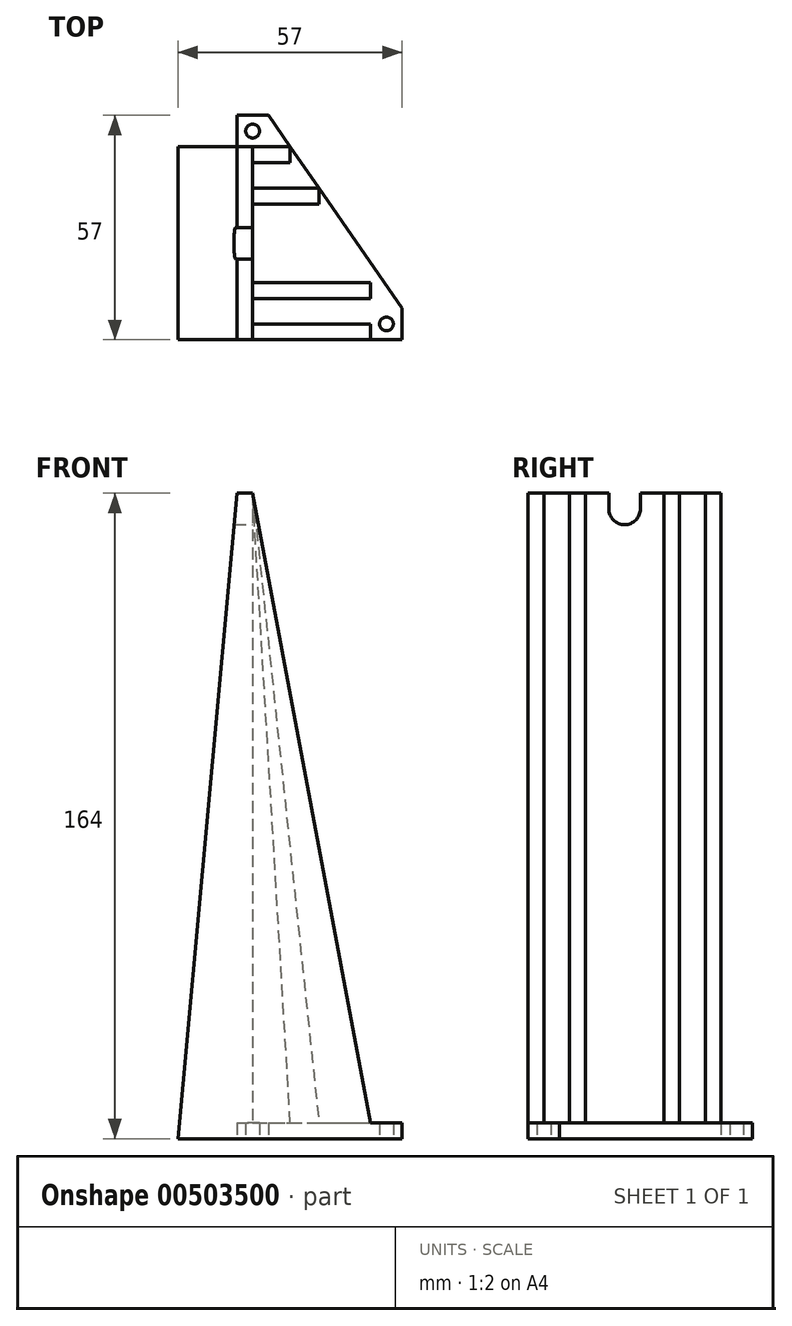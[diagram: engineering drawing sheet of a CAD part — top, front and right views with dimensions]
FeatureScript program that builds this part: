
annotation { "Feature Type Name" : "Feature", "Feature Type Description" : "" }
export const myFeature = defineFeature(function(context is Context, id is Id, definition is map)
    precondition{}
    {
        {
            var Q0;
            Q0=qCreatedBy(makeId("Top.planeOp"),FACE);
            var sketch = newSketch(context, id + "F0", { "sketchPlane" : qUnion([Q0])});
            skCircle(sketch, "E0", {"center": v(0, 0) * mm, "radius": 1.75 * mm});
            skCircle(sketch, "E1", {"center": v(-34, 49) * mm, "radius": 1.75 * mm});
            skLineSegment(sketch, "E2", {"start": v(4, -4) * mm, "end": v(-38, -4) * mm});
            skLineSegment(sketch, "E3", {"start": v(-38, -4) * mm, "end": v(-38, 53) * mm});
            skLineSegment(sketch, "E4", {"start": v(-38, 53) * mm, "end": v(-30, 53) * mm});
            skLineSegment(sketch, "E5", {"start": v(-30, 53) * mm, "end": v(4, 4) * mm});
            skLineSegment(sketch, "E6", {"start": v(4, 4) * mm, "end": v(4, -4) * mm});
            skSolve(sketch);
        }
        {
            var Q0;
            Q0 = qSketchRegion(id + "F0", true);
            extrude(context, id + "F1", {"entities" : qUnion([Q0]), "depth" : 4 * mm});
        }
        {
            var Q0;
            Q0=makeQuery(id+"F1.opExtrude","CAP_FACE",FACE,{"disambiguationData":[OSD([sQuery(id+"F0.wireOp",EDGE,"E0"),sQuery(id+"F0.wireOp",EDGE,"E1"),sQuery(id+"F0.wireOp",EDGE,"E2"),sQuery(id+"F0.wireOp",EDGE,"E3"),sQuery(id+"F0.wireOp",EDGE,"E4"),sQuery(id+"F0.wireOp",EDGE,"E5"),sQuery(id+"F0.wireOp",EDGE,"E6")])],"isStart":false});
            var sketch = newSketch(context, id + "F2", { "sketchPlane" : qUnion([Q0])});
            skLineSegment(sketch, "E7", {"start": v(-38, 45) * mm, "end": v(-24.45, 45) * mm});
            skLineSegment(sketch, "E8", {"start": v(-34, 41) * mm, "end": v(-34, 34.5) * mm});
            skLineSegment(sketch, "E9", {"start": v(-34, 0) * mm, "end": v(-4, 0) * mm});
            skLineSegment(sketch, "E10", {"start": v(-4, 0) * mm, "end": v(-4, -4) * mm});
            skLineSegment(sketch, "E11", {"start": v(-4, -4) * mm, "end": v(-38, -4) * mm});
            skLineSegment(sketch, "E12", {"start": v(-38, -4) * mm, "end": v(-38, 45) * mm});
            skPoint(sketch, "E13", {"position": v(-34, 49) * mm});
            skLineSegment(sketch, "E14", {"start": v(-34, 41) * mm, "end": v(-24.45, 41) * mm});
            skLineSegment(sketch, "E15", {"start": v(-24.45, 41) * mm, "end": v(-24.45, 45) * mm});
            skLineSegment(sketch, "E16", {"start": v(-34, 34.5) * mm, "end": v(-17.16, 34.5) * mm});
            skLineSegment(sketch, "E17", {"start": v(-17.16, 34.5) * mm, "end": v(-17.16, 30.5) * mm});
            skLineSegment(sketch, "E18", {"start": v(-17.16, 30.5) * mm, "end": v(-34, 30.5) * mm});
            skLineSegment(sketch, "E19", {"start": v(-34, 10.5) * mm, "end": v(-4, 10.5) * mm});
            skLineSegment(sketch, "E20", {"start": v(-4, 10.5) * mm, "end": v(-4, 6.5) * mm});
            skLineSegment(sketch, "E21", {"start": v(-4, 6.5) * mm, "end": v(-34, 6.5) * mm});
            skLineSegment(sketch, "E22.trimOffspring", {"start": v(-34, 6.5) * mm, "end": v(-34, 0) * mm});
            skLineSegment(sketch, "E23.trimOffspring", {"start": v(-34, 30.5) * mm, "end": v(-34, 10.5) * mm});
            skLineSegment(sketch, "E24", {"start": v(-38, 20.5) * mm, "end": v(-16.05, 20.5) * mm, "construction": true});
            skSolve(sketch);
        }
        {
            var Q0;
            Q0 = qSketchRegion(id + "F2", true);
            extrude(context, id + "F3", {"entities" : qUnion([Q0]), "operationType" : NewBodyOperationType.ADD, "depth" : 160 * mm});
        }
        {
            var Q0;
            Q0=makeQuery(id+"F3.boolean.opBoolean","MERGE",FACE,{"derivedFrom":[makeQuery(id+"F1.opExtrude","SWEPT_FACE",FACE,{"disambiguationData":[OSD([sQuery(id+"F0.wireOp",EDGE,"E2")])]}),makeQuery(id+"F3.opExtrude","SWEPT_FACE",FACE,{"disambiguationData":[OSD([sQuery(id+"F2.wireOp",EDGE,"E11")])]})]});
            var sketch = newSketch(context, id + "F4", { "sketchPlane" : qUnion([Q0])});
            skLineSegment(sketch, "E25", {"start": v(-38, 0) * mm, "end": v(-53, 0) * mm});
            skLineSegment(sketch, "E26", {"start": v(-53, 0) * mm, "end": v(-38, 164) * mm});
            skLineSegment(sketch, "E27", {"start": v(-38, 164) * mm, "end": v(-38, 0) * mm});
            skSolve(sketch);
        }
        {
            var Q0;
            Q0 = qSketchRegion(id + "F4", true);
            var Q1;
            Q1=makeQuery(id+"F3.opExtrude","SWEPT_FACE",FACE,{"disambiguationData":[OSD([sQuery(id+"F2.wireOp",EDGE,"E7")])]});
            extrude(context, id + "F5", {"entities" : qUnion([Q0]), "operationType" : NewBodyOperationType.ADD, "endBound" : BoundingType.UP_TO_SURFACE, "oppositeDirection" : true, "depth" : 25 * mm, "endBoundEntityFace" : qUnion([Q1]), "offsetDistance" : 25 * mm});
        }
        {
            var Q0;
            Q0=makeQuery(id+"F3.opExtrude","SWEPT_FACE",FACE,{"disambiguationData":[OSD([sQuery(id+"F2.wireOp",EDGE,"E8")])]});
            var sketch = newSketch(context, id + "F6", { "sketchPlane" : qUnion([Q0])});
            skLineSegment(sketch, "E28", {"start": v(20.5, 164) * mm, "end": v(20.5, 160) * mm, "construction": true});
            skArc(sketch, "E29", {"start": v(16.5, 160) * mm, "mid": v(20.5, 156) * mm, "end": v(24.5, 160) * mm});
            skArc(sketch, "E30", {"start": v(24.5, 164) * mm, "mid": v(20.5, 168) * mm, "end": v(16.5, 164) * mm});
            skLineSegment(sketch, "E31", {"start": v(16.5, 164) * mm, "end": v(16.5, 160) * mm});
            skLineSegment(sketch, "E32", {"start": v(24.5, 160) * mm, "end": v(24.5, 164) * mm});
            skLineSegment(sketch, "E33.0", {"start": v(45, 164) * mm, "end": v(45, 4) * mm, "construction": true});
            skLineSegment(sketch, "E34.0", {"start": v(-4, 164) * mm, "end": v(-4, 4) * mm, "construction": true});
            skSolve(sketch);
        }
        {
            var Q0;
            Q0 = qSketchRegion(id + "F6", true);
            extrude(context, id + "F7", {"entities" : qUnion([Q0]), "operationType" : NewBodyOperationType.REMOVE, "endBound" : BoundingType.THROUGH_ALL, "oppositeDirection" : true, "depth" : 25 * mm});
        }
        {
            var Q0;
            Q0=makeQuery(id+"F5.boolean.opBoolean","MERGE",FACE,{"derivedFrom":[makeQuery(id+"F3.boolean.opBoolean","MERGE",FACE,{"derivedFrom":[makeQuery(id+"F1.opExtrude","SWEPT_FACE",FACE,{"disambiguationData":[OSD([sQuery(id+"F0.wireOp",EDGE,"E2")])]}),makeQuery(id+"F3.opExtrude","SWEPT_FACE",FACE,{"disambiguationData":[OSD([sQuery(id+"F2.wireOp",EDGE,"E11")])]})]}),makeQuery(id+"F5.opExtrude","CAP_FACE",FACE,{"disambiguationData":[OSD([sQuery(id+"F4.wireOp",EDGE,"E25"),sQuery(id+"F4.wireOp",EDGE,"E26"),sQuery(id+"F4.wireOp",EDGE,"E27")])],"isStart":true})]});
            var sketch = newSketch(context, id + "F8", { "sketchPlane" : qUnion([Q0])});
            skLineSegment(sketch, "E35", {"start": v(-4, 4) * mm, "end": v(-34, 164) * mm});
            skLineSegment(sketch, "E36", {"start": v(-34, 164) * mm, "end": v(-4, 164) * mm});
            skLineSegment(sketch, "E37", {"start": v(-4, 164) * mm, "end": v(-4, 4) * mm});
            skSolve(sketch);
        }
        {
            var Q0;
            Q0 = qSketchRegion(id + "F8", true);
            var Q1;
            Q1=makeQuery(id+"F3.opExtrude","SWEPT_FACE",FACE,{"disambiguationData":[OSD([sQuery(id+"F2.wireOp",EDGE,"E19")])]});
            extrude(context, id + "F9", {"entities" : qUnion([Q0]), "operationType" : NewBodyOperationType.REMOVE, "endBound" : BoundingType.UP_TO_SURFACE, "oppositeDirection" : true, "depth" : 25 * mm, "endBoundEntityFace" : qUnion([Q1]), "offsetDistance" : 25 * mm});
        }
        {
            var Q0;
            Q0=makeQuery(id+"F3.opExtrude","SWEPT_FACE",FACE,{"disambiguationData":[OSD([sQuery(id+"F2.wireOp",EDGE,"E18")])]});
            var sketch = newSketch(context, id + "F10", { "sketchPlane" : qUnion([Q0])});
            skLineSegment(sketch, "E38", {"start": v(-34, 164) * mm, "end": v(-17.16, 4) * mm});
            skLineSegment(sketch, "E39", {"start": v(-17.16, 4) * mm, "end": v(-17.16, 164) * mm});
            skLineSegment(sketch, "E40", {"start": v(-17.16, 164) * mm, "end": v(-34, 164) * mm});
            skSolve(sketch);
        }
        {
            var Q0;
            Q0 = qSketchRegion(id + "F10", true);
            var Q1;
            Q1=makeQuery(id+"F3.opExtrude","SWEPT_FACE",FACE,{"disambiguationData":[OSD([sQuery(id+"F2.wireOp",EDGE,"E16")])]});
            extrude(context, id + "F11", {"entities" : qUnion([Q0]), "operationType" : NewBodyOperationType.REMOVE, "endBound" : BoundingType.UP_TO_SURFACE, "oppositeDirection" : true, "depth" : 25 * mm, "endBoundEntityFace" : qUnion([Q1]), "offsetDistance" : 25 * mm});
        }
        {
            var Q0;
            Q0=makeQuery(id+"F3.opExtrude","SWEPT_FACE",FACE,{"disambiguationData":[OSD([sQuery(id+"F2.wireOp",EDGE,"E14")])]});
            var sketch = newSketch(context, id + "F12", { "sketchPlane" : qUnion([Q0])});
            skLineSegment(sketch, "E41", {"start": v(-24.45, 4) * mm, "end": v(-34, 164) * mm});
            skLineSegment(sketch, "E42", {"start": v(-34, 164) * mm, "end": v(-24.45, 164) * mm});
            skLineSegment(sketch, "E43", {"start": v(-24.45, 164) * mm, "end": v(-24.45, 4) * mm});
            skSolve(sketch);
        }
        {
            var Q0;
            Q0 = qSketchRegion(id + "F12", true);
            var Q1;
            {var subQ0=sQuery(id+"F2.wireOp",EDGE,"E7");Q1=makeQuery(id+"F5.boolean.opBoolean","MERGE",FACE,{"derivedFrom":[makeQuery(id+"F3.opExtrude","SWEPT_FACE",FACE,{"disambiguationData":[OSD([subQ0])]}),makeQuery(id+"F5.opExtrude","CAP_FACE",FACE,{"disambiguationData":[OSD([subQ0])],"isStart":false})]});}
            extrude(context, id + "F13", {"entities" : qUnion([Q0]), "operationType" : NewBodyOperationType.REMOVE, "endBound" : BoundingType.UP_TO_SURFACE, "oppositeDirection" : true, "depth" : 25 * mm, "endBoundEntityFace" : qUnion([Q1]), "offsetDistance" : 25 * mm});
        }
    });
